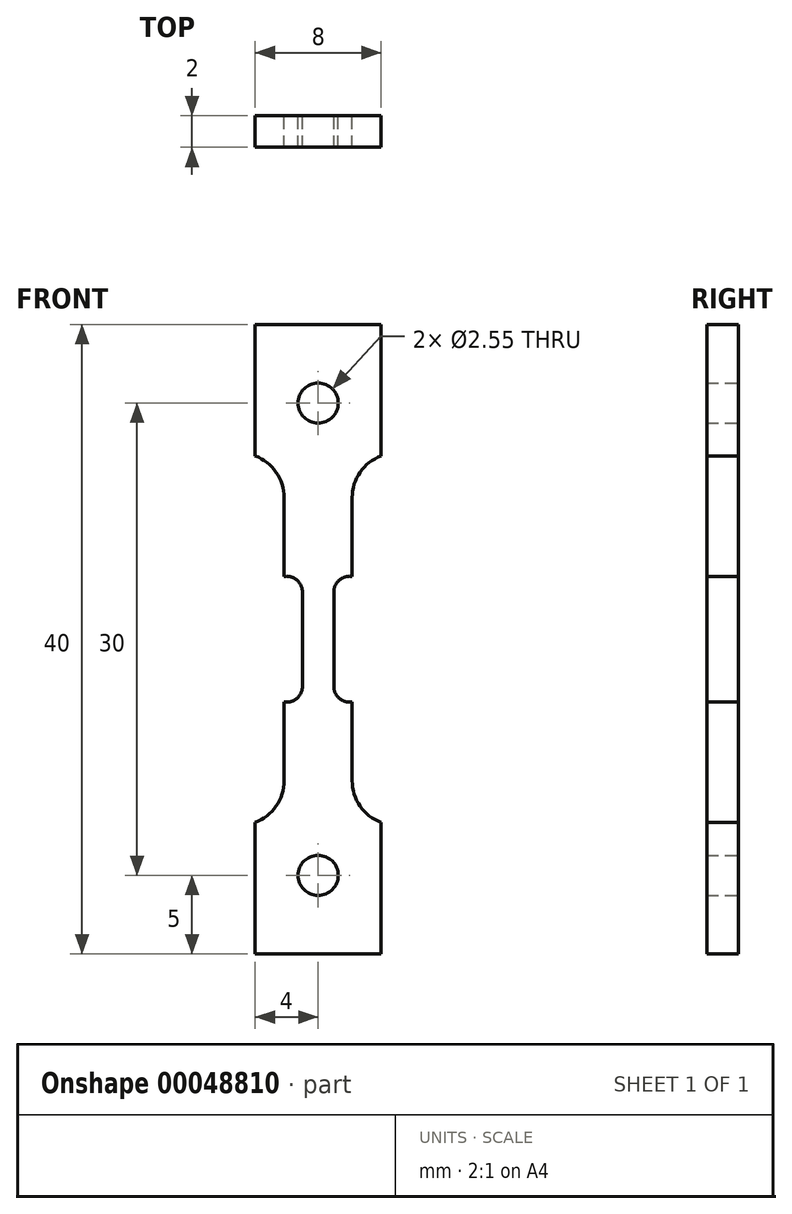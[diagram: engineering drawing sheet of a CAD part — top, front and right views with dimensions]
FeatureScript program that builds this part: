
annotation { "Feature Type Name" : "Feature", "Feature Type Description" : "" }
export const myFeature = defineFeature(function(context is Context, id is Id, definition is map)
    precondition{}
    {
        {
            assignVariable(context, id + "F0", {"variableType" : VariableType.LENGTH, "name" : "thickness", "lengthValue" : 2 * mm});
        }
        {
            var Q0;
            Q0=qCreatedBy(makeId("Front.planeOp"),FACE);
            var sketch = newSketch(context, id + "F1", { "sketchPlane" : qUnion([Q0])});
            skLineSegment(sketch, "E0", {"start": v(4, 20) * mm, "end": v(4, 11.64) * mm});
            skArc(sketch, "E1", {"start": v(2.16, 8.99) * mm, "mid": v(2.67, 10.6) * mm, "end": v(4, 11.64) * mm});
            skLineSegment(sketch, "E2", {"start": v(4, 20) * mm, "end": v(0, 20) * mm});
            skLineSegment(sketch, "E3.MirrorCS", {"start": v(-4, 20) * mm, "end": v(0, 20) * mm});
            skLineSegment(sketch, "E4.MirrorCS", {"start": v(-4, 20) * mm, "end": v(-4, 11.64) * mm});
            skArc(sketch, "E5.MirrorCS", {"start": v(-2.16, 8.99) * mm, "mid": v(-2.67, 10.6) * mm, "end": v(-4, 11.64) * mm});
            skPoint(sketch, "E6", {"position": v(0, 15) * mm});
            skCircle(sketch, "E7", {"center": v(0, 15) * mm, "radius": 1.27 * mm});
            skLineSegment(sketch, "E8", {"start": v(-1, 0) * mm, "end": v(-1, 3) * mm});
            skLineSegment(sketch, "E9.MirrorCS", {"start": v(1, 0) * mm, "end": v(1, 3) * mm});
            skArc(sketch, "E10", {"start": v(-1, 3) * mm, "mid": v(-1.35, 3.76) * mm, "end": v(-2.16, 3.99) * mm});
            skArc(sketch, "E11.MirrorCS", {"start": v(1, 3) * mm, "mid": v(1.35, 3.76) * mm, "end": v(2.16, 3.99) * mm});
            skLineSegment(sketch, "E12", {"start": v(-2.16, 8.99) * mm, "end": v(-2.16, 3.99) * mm});
            skLineSegment(sketch, "E13.MirrorCS", {"start": v(2.16, 8.99) * mm, "end": v(2.16, 3.99) * mm});
            skArc(sketch, "E14.MirrorCS", {"start": v(2.16, -8.99) * mm, "mid": v(2.67, -10.6) * mm, "end": v(4, -11.64) * mm});
            skLineSegment(sketch, "E15.MirrorCS", {"start": v(1, 0) * mm, "end": v(1, -3) * mm});
            skLineSegment(sketch, "E16.MirrorCS", {"start": v(4, -20) * mm, "end": v(4, -11.64) * mm});
            skLineSegment(sketch, "E17.MirrorCS", {"start": v(-2.16, -8.99) * mm, "end": v(-2.16, -3.99) * mm});
            skArc(sketch, "E18.MirrorCS", {"start": v(1, -3) * mm, "mid": v(1.35, -3.76) * mm, "end": v(2.16, -3.99) * mm});
            skLineSegment(sketch, "E19.MirrorCS", {"start": v(-1, 0) * mm, "end": v(-1, -3) * mm});
            skCircle(sketch, "E20.MirrorC", {"center": v(0, -15) * mm, "radius": 1.27 * mm});
            skArc(sketch, "E21.MirrorCS", {"start": v(-2.16, -8.99) * mm, "mid": v(-2.67, -10.6) * mm, "end": v(-4, -11.64) * mm});
            skLineSegment(sketch, "E22.MirrorCS", {"start": v(2.16, -8.99) * mm, "end": v(2.16, -3.99) * mm});
            skLineSegment(sketch, "E23.MirrorCS", {"start": v(4, -20) * mm, "end": v(0, -20) * mm});
            skArc(sketch, "E24.MirrorCS", {"start": v(-1, -3) * mm, "mid": v(-1.35, -3.76) * mm, "end": v(-2.16, -3.99) * mm});
            skLineSegment(sketch, "E25.MirrorCS", {"start": v(-4, -20) * mm, "end": v(0, -20) * mm});
            skLineSegment(sketch, "E26.MirrorCS", {"start": v(-4, -20) * mm, "end": v(-4, -11.64) * mm});
            skSolve(sketch);
        }
        {
            var Q0;
            Q0=makeQuery(id+"F1.imprint","IMPRINT",FACE,{"disambiguationData":[TD([[makeQuery(id+"F1.imprint","IMPRINT",EDGE,{"derivedFrom":sQuery(id+"F1.wireOp",EDGE,"E0")}),-1.0]])]});
            extrude(context, id + "F2", {"entities" : qUnion([Q0]), "offsetDistance" : 25 * mm, "depth" : getVariable(context, 'thickness'), "symmetric" : true});
        }
    });
